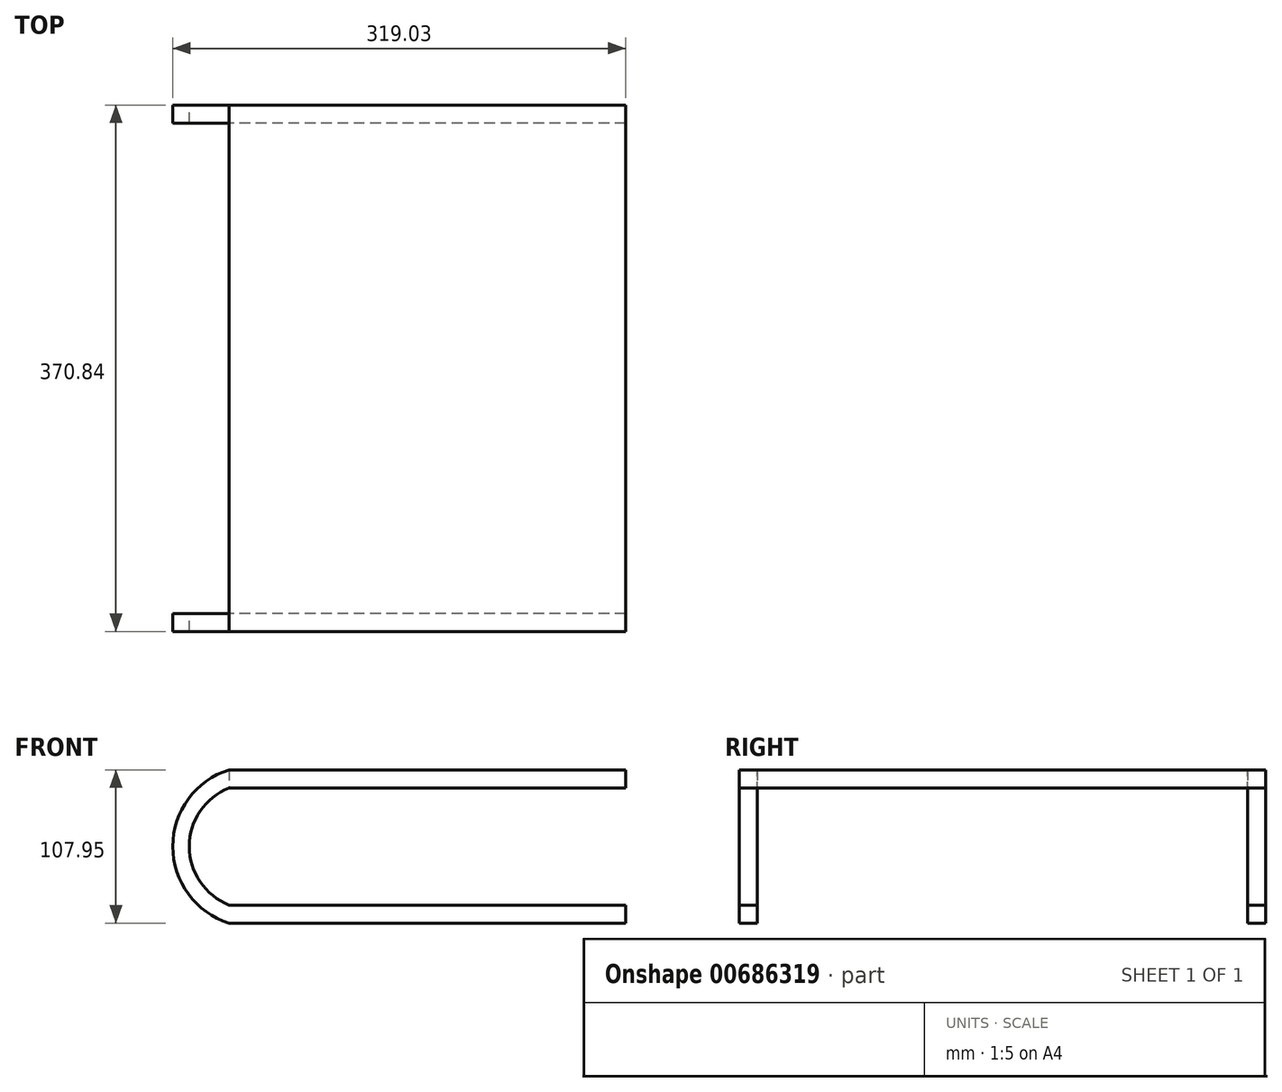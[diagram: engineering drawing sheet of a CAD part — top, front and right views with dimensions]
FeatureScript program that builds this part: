
annotation { "Feature Type Name" : "Feature", "Feature Type Description" : "" }
export const myFeature = defineFeature(function(context is Context, id is Id, definition is map)
    precondition{}
    {
        {
            var Q0;
            Q0=qCreatedBy(makeId("Top.planeOp"),FACE);
            var sketch = newSketch(context, id + "F0", { "sketchPlane" : qUnion([Q0])});
            skLineSegment(sketch, "E0.bottom", {"start": v(-139.7, -185.42) * mm, "end": v(139.7, -185.42) * mm});
            skLineSegment(sketch, "E0.top", {"start": v(-139.7, 185.42) * mm, "end": v(139.7, 185.42) * mm});
            skLineSegment(sketch, "E0.left", {"start": v(-139.7, -185.42) * mm, "end": v(-139.7, 185.42) * mm});
            skLineSegment(sketch, "E0.right", {"start": v(139.7, -185.42) * mm, "end": v(139.7, 185.42) * mm});
            skPoint(sketch, "E0.middle", {"position": v(0, 0) * mm});
            skSolve(sketch);
        }
        {
            var Q0;
            Q0 = qSketchRegion(id + "F0", true);
            extrude(context, id + "F1", {"entities" : qUnion([Q0]), "depth" : 12.7 * mm, "offsetDistance" : 25.4 * mm});
        }
        {
            var Q0;
            Q0=makeQuery(id+"F1.opExtrude","SWEPT_FACE",FACE,{"disambiguationData":[OSD([sQuery(id+"F0.wireOp",EDGE,"E0.top")])]});
            var sketch = newSketch(context, id + "F2", { "sketchPlane" : qUnion([Q0])});
            skLineSegment(sketch, "E1", {"start": v(-139.7, -95.25) * mm, "end": v(139.7, -95.25) * mm});
            skArc(sketch, "E2", {"start": v(139.7, -95.25) * mm, "mid": v(179.33, -41.27) * mm, "end": v(139.7, 12.7) * mm});
            skLineSegment(sketch, "E3", {"start": v(139.7, -82.55) * mm, "end": v(-139.7, -82.55) * mm});
            skLineSegment(sketch, "E4", {"start": v(-139.7, -82.55) * mm, "end": v(-139.7, -95.25) * mm});
            skArc(sketch, "E5", {"start": v(139.7, -82.55) * mm, "mid": v(167.71, -41.27) * mm, "end": v(139.7, 0) * mm});
            skSolve(sketch);
        }
        {
            var Q0;
            Q0=makeQuery(id+"F2.imprint","IMPRINT",FACE,{"disambiguationData":[TD([[makeQuery(id+"F2.imprint","IMPRINT",EDGE,{"derivedFrom":sQuery(id+"F2.wireOp",EDGE,"E1")}),1.0]])]});
            extrude(context, id + "F3", {"entities" : qUnion([Q0]), "operationType" : NewBodyOperationType.ADD, "oppositeDirection" : true, "depth" : 12.7 * mm, "offsetDistance" : 25.4 * mm});
        }
        {
            var Q0;
            Q0=makeQuery(id+"F2.imprint","IMPRINT",FACE,{"disambiguationData":[TD([[makeQuery(id+"F2.imprint","IMPRINT",EDGE,{"derivedFrom":sQuery(id+"F2.wireOp",EDGE,"E1")}),1.0]])]});
            extrude(context, id + "F4", {"entities" : qUnion([Q0]), "operationType" : NewBodyOperationType.ADD, "oppositeDirection" : true, "depth" : 370.84 * mm, "offsetDistance" : 25.4 * mm, "hasSecondDirection" : true, "secondDirectionOppositeDirection" : true, "secondDirectionDepth" : 358.14 * mm});
        }
    });
